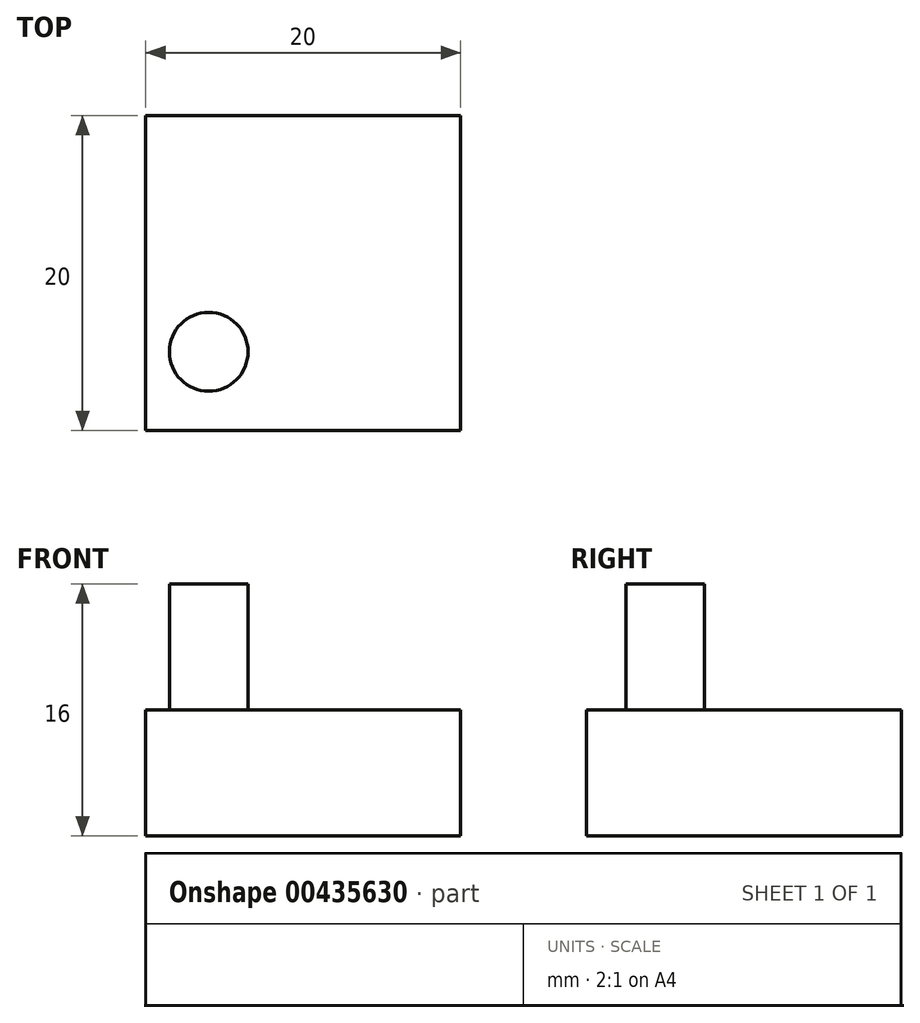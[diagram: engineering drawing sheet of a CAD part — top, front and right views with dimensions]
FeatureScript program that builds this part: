
annotation { "Feature Type Name" : "Feature", "Feature Type Description" : "" }
export const myFeature = defineFeature(function(context is Context, id is Id, definition is map)
    precondition{}
    {
        {
            var Q0;
            Q0=qCreatedBy(makeId("Top.planeOp"),FACE);
            var sketch = newSketch(context, id + "F0", { "sketchPlane" : qUnion([Q0])});
            skLineSegment(sketch, "E0.bottom", {"start": v(-10, 10) * mm, "end": v(10, 10) * mm});
            skLineSegment(sketch, "E0.top", {"start": v(-10, -10) * mm, "end": v(10, -10) * mm});
            skLineSegment(sketch, "E0.left", {"start": v(-10, 10) * mm, "end": v(-10, -10) * mm});
            skLineSegment(sketch, "E0.right", {"start": v(10, 10) * mm, "end": v(10, -10) * mm});
            skPoint(sketch, "E0.middle", {"position": v(0, 0) * mm});
            skSolve(sketch);
        }
        {
            var Q0;
            Q0=makeQuery(id+"F0.imprint","IMPRINT",FACE,{"disambiguationData":[TD([[makeQuery(id+"F0.imprint","IMPRINT",EDGE,{"derivedFrom":sQuery(id+"F0.wireOp",EDGE,"E0.bottom")}),-1.0]])]});
            var sketch = newSketch(context, id + "F1", { "sketchPlane" : qUnion([Q0])});
            skLineSegment(sketch, "E1", {"start": v(0, 0) * mm, "end": v(0, -5) * mm});
            skLineSegment(sketch, "E2", {"start": v(0, -5) * mm, "end": v(-6, -5) * mm});
            skCircle(sketch, "E3", {"center": v(-6, -5) * mm, "radius": 2.5 * mm});
            skSolve(sketch);
        }
        {
            var Q0;
            Q0=qSketchRegion(id+"F1",true);
            extrude(context, id + "F2", {"entities" : qUnion([Q0]), "depth" : 8 * mm});
        }
        {
            var Q0;
            Q0=makeQuery(id+"F0.imprint","IMPRINT",FACE,{"disambiguationData":[TD([[makeQuery(id+"F0.imprint","IMPRINT",EDGE,{"derivedFrom":sQuery(id+"F0.wireOp",EDGE,"E0.bottom")}),-1.0]])]});
            extrude(context, id + "F3", {"entities" : qUnion([Q0]), "operationType" : NewBodyOperationType.ADD, "oppositeDirection" : true, "depth" : 8 * mm});
        }
    });
